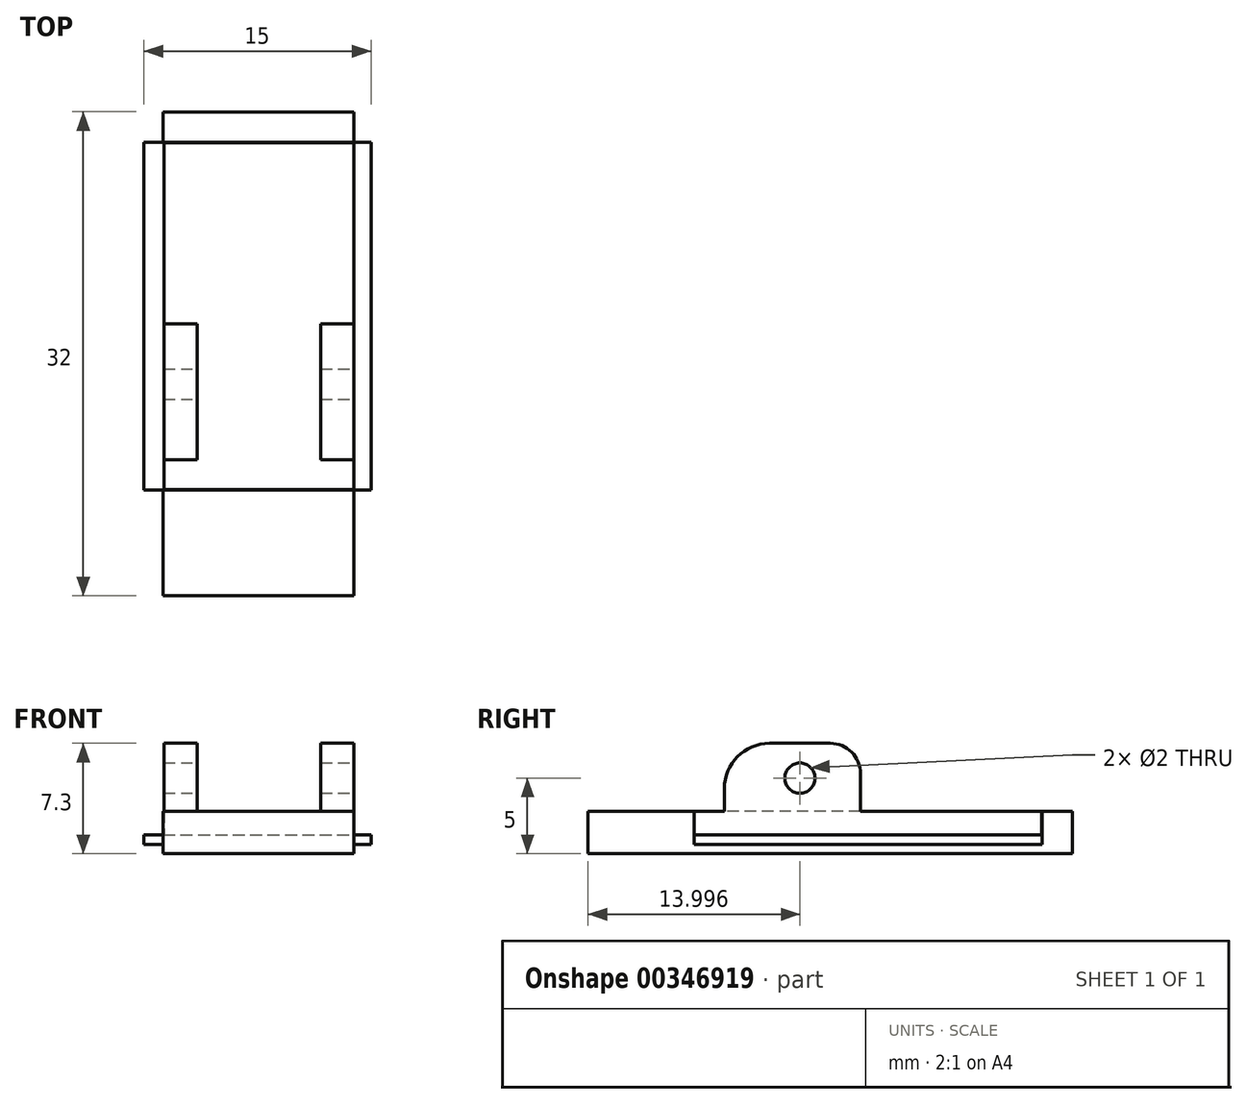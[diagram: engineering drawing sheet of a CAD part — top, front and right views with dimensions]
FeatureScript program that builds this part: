
annotation { "Feature Type Name" : "Feature", "Feature Type Description" : "" }
export const myFeature = defineFeature(function(context is Context, id is Id, definition is map)
    precondition{}
    {
        {
            var Q0;
            Q0=qCreatedBy(makeId("Top.planeOp"),FACE);
            var sketch = newSketch(context, id + "F0", { "sketchPlane" : qUnion([Q0])});
            skLineSegment(sketch, "E0.bottom", {"start": v(-6.16, 12.6) * mm, "end": v(6.44, 12.6) * mm});
            skLineSegment(sketch, "E0.top", {"start": v(-6.16, -19.4) * mm, "end": v(6.44, -19.4) * mm});
            skLineSegment(sketch, "E0.left", {"start": v(-6.16, 12.6) * mm, "end": v(-6.16, -19.4) * mm});
            skLineSegment(sketch, "E0.right", {"start": v(6.44, 12.6) * mm, "end": v(6.44, -19.4) * mm});
            skSolve(sketch);
        }
        {
            var Q0;
            Q0 = qSketchRegion(id + "F0", true);
            extrude(context, id + "F1", {"entities" : qUnion([Q0]), "depth" : .6 * mm});
        }
        {
            var Q0;
            Q0=makeQuery(id+"F1.opExtrude","CAP_FACE",FACE,{"disambiguationData":[OSD([sQuery(id+"F0.wireOp",EDGE,"E0.bottom"),sQuery(id+"F0.wireOp",EDGE,"E0.top"),sQuery(id+"F0.wireOp",EDGE,"E0.left"),sQuery(id+"F0.wireOp",EDGE,"E0.right")])],"isStart":false});
            var sketch = newSketch(context, id + "F2", { "sketchPlane" : qUnion([Q0])});
            skLineSegment(sketch, "E1.bottom", {"start": v(-7.43, 10.6) * mm, "end": v(7.57, 10.6) * mm});
            skLineSegment(sketch, "E1.top", {"start": v(-7.43, -12.4) * mm, "end": v(7.57, -12.4) * mm});
            skLineSegment(sketch, "E1.left", {"start": v(-7.43, 10.6) * mm, "end": v(-7.43, -12.4) * mm});
            skLineSegment(sketch, "E1.right", {"start": v(7.57, 10.6) * mm, "end": v(7.57, -12.4) * mm});
            skSolve(sketch);
        }
        {
            var Q0;
            Q0 = qSketchRegion(id + "F2", true);
            extrude(context, id + "F3", {"entities" : qUnion([Q0]), "operationType" : NewBodyOperationType.ADD, "depth" : .66 * mm});
        }
        {
            var Q0;
            {var subQ0=sQuery(id+"F0.wireOp",EDGE,"E0.right");var subQ2=sQuery(id+"F0.wireOp",EDGE,"E0.left");var subQ3=sQuery(id+"F0.wireOp",EDGE,"E0.top");Q0=makeQuery(id+"F3.boolean.opBoolean","SPLIT",FACE,{"disambiguationData":[TD([makeQuery(id+"F1.opExtrude","SWEPT_FACE",FACE,{"disambiguationData":[OSD([subQ3])]})])],"derivedFrom":makeQuery(id+"F1.opExtrude","CAP_FACE",FACE,{"disambiguationData":[OSD([sQuery(id+"F0.wireOp",EDGE,"E0.bottom"),subQ3,subQ2,subQ0])],"isStart":false})});}
            var sketch = newSketch(context, id + "F4", { "sketchPlane" : qUnion([Q0])});
            skLineSegment(sketch, "E2.bottom", {"start": v(-6.16, -12.4) * mm, "end": v(6.44, -12.4) * mm});
            skLineSegment(sketch, "E2.top", {"start": v(-6.16, -19.4) * mm, "end": v(6.44, -19.4) * mm});
            skLineSegment(sketch, "E2.left", {"start": v(-6.16, -12.4) * mm, "end": v(-6.16, -19.4) * mm});
            skLineSegment(sketch, "E2.right", {"start": v(6.44, -12.4) * mm, "end": v(6.44, -19.4) * mm});
            skSolve(sketch);
        }
        {
            var Q0;
            Q0 = qSketchRegion(id + "F4", true);
            extrude(context, id + "F5", {"entities" : qUnion([Q0]), "operationType" : NewBodyOperationType.ADD, "depth" : 2.2 * mm});
        }
        {
            var Q0;
            {var subQ1=sQuery(id+"F0.wireOp",EDGE,"E0.left");var subQ2=sQuery(id+"F0.wireOp",EDGE,"E0.right");var subQ3=sQuery(id+"F0.wireOp",EDGE,"E0.bottom");Q0=makeQuery(id+"F3.boolean.opBoolean","SPLIT",FACE,{"disambiguationData":[TD([makeQuery(id+"F1.opExtrude","SWEPT_FACE",FACE,{"disambiguationData":[OSD([subQ3])]})])],"derivedFrom":makeQuery(id+"F1.opExtrude","CAP_FACE",FACE,{"disambiguationData":[OSD([subQ3,sQuery(id+"F0.wireOp",EDGE,"E0.top"),subQ1,subQ2])],"isStart":false})});}
            var sketch = newSketch(context, id + "F6", { "sketchPlane" : qUnion([Q0])});
            skLineSegment(sketch, "E3.bottom", {"start": v(-6.16, 12.6) * mm, "end": v(6.44, 12.6) * mm});
            skLineSegment(sketch, "E3.top", {"start": v(-6.16, 10.6) * mm, "end": v(6.44, 10.6) * mm});
            skLineSegment(sketch, "E3.left", {"start": v(-6.16, 12.6) * mm, "end": v(-6.16, 10.6) * mm});
            skLineSegment(sketch, "E3.right", {"start": v(6.44, 12.6) * mm, "end": v(6.44, 10.6) * mm});
            skSolve(sketch);
        }
        {
            var Q0;
            Q0 = qSketchRegion(id + "F6", true);
            extrude(context, id + "F7", {"entities" : qUnion([Q0]), "operationType" : NewBodyOperationType.ADD, "depth" : 2.2 * mm});
        }
        {
            var Q0;
            Q0=makeQuery(id+"F3.opExtrude","CAP_FACE",FACE,{"disambiguationData":[OSD([sQuery(id+"F2.wireOp",EDGE,"E1.bottom"),sQuery(id+"F2.wireOp",EDGE,"E1.top"),sQuery(id+"F2.wireOp",EDGE,"E1.left"),sQuery(id+"F2.wireOp",EDGE,"E1.right")])],"isStart":false});
            var sketch = newSketch(context, id + "F8", { "sketchPlane" : qUnion([Q0])});
            skLineSegment(sketch, "E4.bottom", {"start": v(-6.16, 10.6) * mm, "end": v(6.44, 10.6) * mm});
            skLineSegment(sketch, "E4.top", {"start": v(-6.16, -12.4) * mm, "end": v(6.44, -12.4) * mm});
            skLineSegment(sketch, "E4.left", {"start": v(-6.16, 10.6) * mm, "end": v(-6.16, -12.4) * mm});
            skLineSegment(sketch, "E4.right", {"start": v(6.44, 10.6) * mm, "end": v(6.44, -12.4) * mm});
            skSolve(sketch);
        }
        {
            var Q0;
            Q0=makeQuery(id+"F8.imprint","IMPRINT",FACE,{"disambiguationData":[TD([[makeQuery(id+"F8.imprint","IMPRINT",EDGE,{"derivedFrom":sQuery(id+"F8.wireOp",EDGE,"E4.bottom")}),-1.0]])]});
            var sketch = newSketch(context, id + "F9", { "sketchPlane" : qUnion([Q0])});
            skLineSegment(sketch, "E5.bottom", {"start": v(-6.12, 10.57) * mm, "end": v(6.45, 10.57) * mm});
            skLineSegment(sketch, "E5.top", {"start": v(-6.12, -12.38) * mm, "end": v(6.45, -12.38) * mm});
            skLineSegment(sketch, "E5.left", {"start": v(-6.12, 10.57) * mm, "end": v(-6.12, -12.38) * mm});
            skLineSegment(sketch, "E5.right", {"start": v(6.45, 10.57) * mm, "end": v(6.45, -12.38) * mm});
            skSolve(sketch);
        }
        {
            var Q0;
            Q0 = qSketchRegion(id + "F9", true);
            extrude(context, id + "F10", {"entities" : qUnion([Q0]), "operationType" : NewBodyOperationType.ADD, "depth" : 1.54 * mm});
        }
        {
            var Q0;
            Q0=makeQuery(id+"F10.opExtrude","CAP_FACE",FACE,{"disambiguationData":[OSD([sQuery(id+"F9.wireOp",EDGE,"E5.bottom"),sQuery(id+"F9.wireOp",EDGE,"E5.top"),sQuery(id+"F9.wireOp",EDGE,"E5.left"),sQuery(id+"F9.wireOp",EDGE,"E5.right")])],"isStart":false});
            var sketch = newSketch(context, id + "F11", { "sketchPlane" : qUnion([Q0])});
            skLineSegment(sketch, "E6.bottom", {"start": v(-6.12, -1.4) * mm, "end": v(-3.92, -1.4) * mm});
            skLineSegment(sketch, "E6.top", {"start": v(-6.12, -10.4) * mm, "end": v(-3.92, -10.4) * mm});
            skLineSegment(sketch, "E6.left", {"start": v(-6.12, -1.4) * mm, "end": v(-6.12, -10.4) * mm});
            skLineSegment(sketch, "E6.right", {"start": v(-3.92, -1.4) * mm, "end": v(-3.92, -10.4) * mm});
            skLineSegment(sketch, "E7.bottom", {"start": v(6.45, -1.4) * mm, "end": v(4.25, -1.4) * mm});
            skLineSegment(sketch, "E7.top", {"start": v(6.45, -10.4) * mm, "end": v(4.25, -10.4) * mm});
            skLineSegment(sketch, "E7.left", {"start": v(6.45, -1.4) * mm, "end": v(6.45, -10.4) * mm});
            skLineSegment(sketch, "E7.right", {"start": v(4.25, -1.4) * mm, "end": v(4.25, -10.4) * mm});
            skSolve(sketch);
        }
        {
            var Q0;
            Q0 = qSketchRegion(id + "F11", true);
            extrude(context, id + "F12", {"entities" : qUnion([Q0]), "operationType" : NewBodyOperationType.ADD, "depth" : 4.5 * mm});
        }
        {
            var Q0;
            Q0=makeQuery(id+"F12.boolean.opBoolean","MERGE",FACE,{"derivedFrom":[makeQuery(id+"F10.opExtrude","SWEPT_FACE",FACE,{"disambiguationData":[OSD([sQuery(id+"F9.wireOp",EDGE,"E5.right")])]}),makeQuery(id+"F12.opExtrude","SWEPT_FACE",FACE,{"disambiguationData":[OSD([sQuery(id+"F11.wireOp",EDGE,"E7.left")])]})]});
            var sketch = newSketch(context, id + "F13", { "sketchPlane" : qUnion([Q0])});
            skCircle(sketch, "E8", {"center": v(-5.4, 5) * mm, "radius": 1 * mm});
            skSolve(sketch);
        }
        {
            var Q0;
            Q0 = qSketchRegion(id + "F13", true);
            extrude(context, id + "F14", {"entities" : qUnion([Q0]), "operationType" : NewBodyOperationType.REMOVE, "oppositeDirection" : true, "depth" : 16 * mm});
        }
        {
            var Q0;
            Q0=makeQuery(id+"F12.opExtrude","CAP_EDGE",EDGE,{"disambiguationData":[OSD([sQuery(id+"F11.wireOp",EDGE,"E6.top")])],"isStart":false});
            fillet(context, id + "F15", {"entities" : qUnion([Q0]), "radius" : 3 * mm, "tangentPropagation" : true, "allowEdgeOverflow" : false});
        }
        {
            var Q0;
            Q0=makeQuery(id+"F12.opExtrude","CAP_EDGE",EDGE,{"disambiguationData":[OSD([sQuery(id+"F11.wireOp",EDGE,"E6.bottom")])],"isStart":false});
            fillet(context, id + "F16", {"entities" : qUnion([Q0]), "radius" : 2 * mm, "tangentPropagation" : true, "allowEdgeOverflow" : false});
        }
        {
            var Q0;
            Q0=makeQuery(id+"F12.opExtrude","CAP_EDGE",EDGE,{"disambiguationData":[OSD([sQuery(id+"F11.wireOp",EDGE,"E7.top")])],"isStart":false});
            fillet(context, id + "F17", {"entities" : qUnion([Q0]), "radius" : 3 * mm, "tangentPropagation" : true, "allowEdgeOverflow" : false});
        }
        {
            var Q0;
            Q0=makeQuery(id+"F12.opExtrude","CAP_EDGE",EDGE,{"disambiguationData":[OSD([sQuery(id+"F11.wireOp",EDGE,"E7.bottom")])],"isStart":false});
            fillet(context, id + "F18", {"entities" : qUnion([Q0]), "radius" : 2 * mm, "tangentPropagation" : true, "allowEdgeOverflow" : false});
        }
    });
